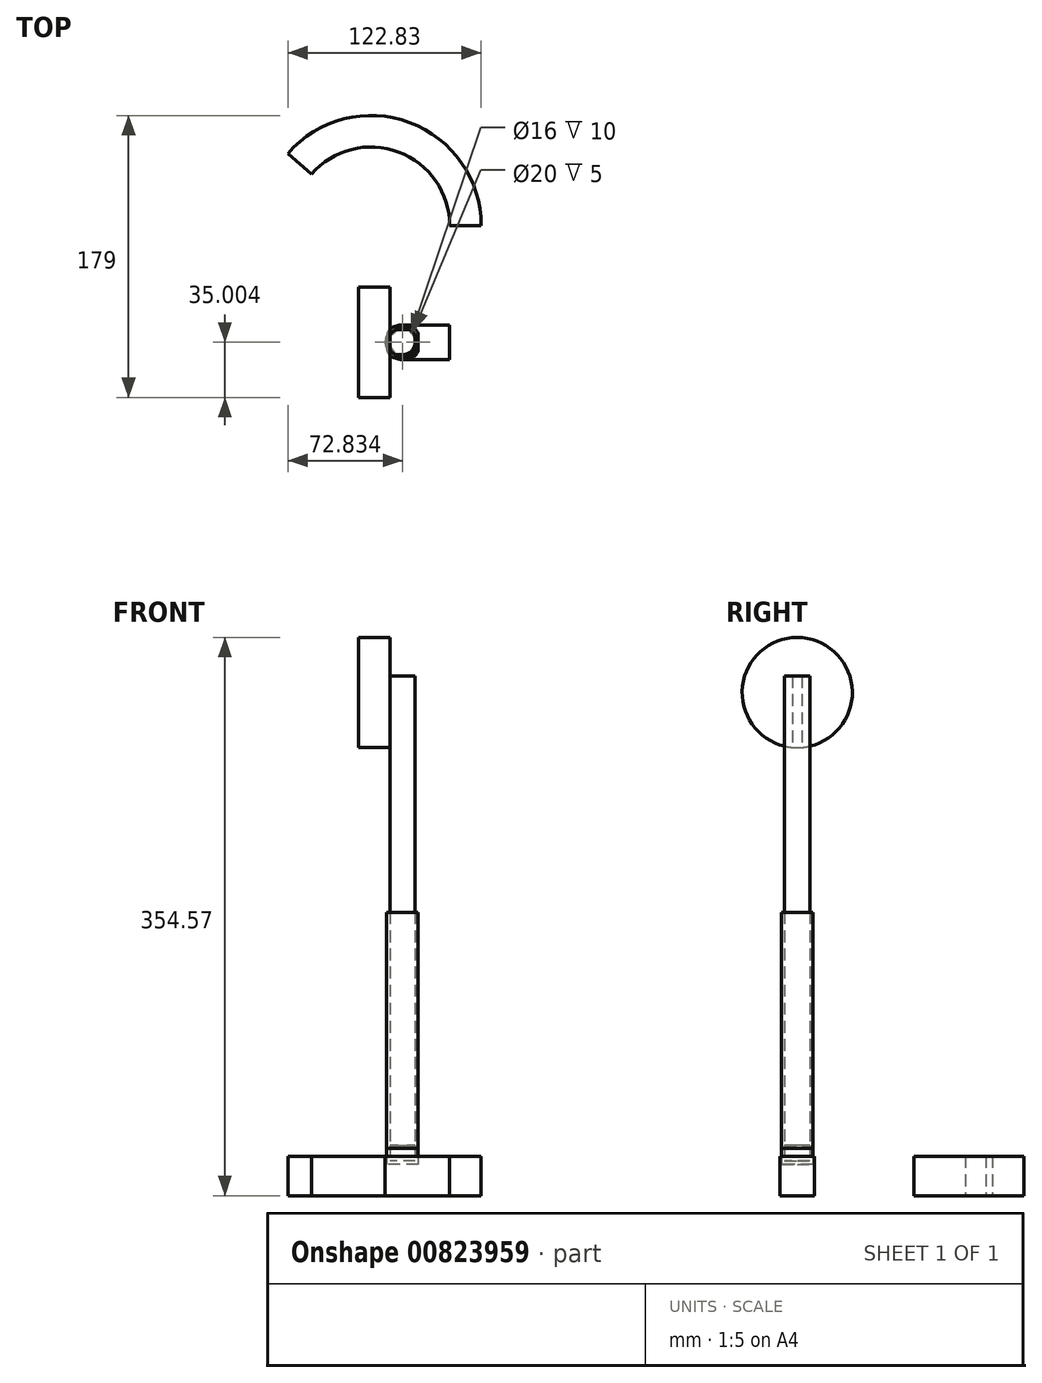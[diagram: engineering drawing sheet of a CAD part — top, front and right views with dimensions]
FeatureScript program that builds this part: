
annotation { "Feature Type Name" : "Feature", "Feature Type Description" : "" }
export const myFeature = defineFeature(function(context is Context, id is Id, definition is map)
    precondition{}
    {
        {
            var Q0;
            Q0=qCreatedBy(makeId("Top.planeOp"),FACE);
            var sketch = newSketch(context, id + "F0", { "sketchPlane" : qUnion([Q0])});
            skLineSegment(sketch, "E0.bottom", {"start": v(17.96, 119.9) * mm, "end": v(67.96, 119.9) * mm});
            skLineSegment(sketch, "E0.left", {"start": v(17.96, 119.9) * mm, "end": v(17.96, -30.1) * mm});
            skLineSegment(sketch, "E0.right", {"start": v(117.96, 119.9) * mm, "end": v(117.96, -30.1) * mm});
            skArc(sketch, "E1", {"start": v(117.96, 119.9) * mm, "mid": v(85.47, 166.74) * mm, "end": v(30.23, 152.7) * mm});
            skArc(sketch, "E2.MirrorCS", {"start": v(117.96, -30.1) * mm, "mid": v(85.47, -76.93) * mm, "end": v(30.23, -62.9) * mm});
            skArc(sketch, "E3.0", {"start": v(137.96, 119.9) * mm, "mid": v(92.48, 185.47) * mm, "end": v(15.13, 165.83) * mm});
            skLineSegment(sketch, "E3.1", {"start": v(137.96, 119.9) * mm, "end": v(137.96, -30.1) * mm});
            skArc(sketch, "E3.2", {"start": v(137.96, -30.1) * mm, "mid": v(92.48, -95.66) * mm, "end": v(15.13, -76.02) * mm});
            skLineSegment(sketch, "E4", {"start": v(67.96, 119.9) * mm, "end": v(-3.53, 182.05) * mm});
            skLineSegment(sketch, "E5.MirrorCS", {"start": v(67.96, -30.1) * mm, "end": v(-3.53, -92.24) * mm});
            skLineSegment(sketch, "E6.trimOffspring", {"start": v(117.96, 119.9) * mm, "end": v(137.96, 119.9) * mm});
            skArc(sketch, "E7", {"start": v(87.96, 56.9) * mm, "mid": v(76.96, 45.9) * mm, "end": v(87.96, 34.9) * mm});
            skLineSegment(sketch, "E8", {"start": v(117.96, 56.9) * mm, "end": v(87.96, 56.9) * mm});
            skLineSegment(sketch, "E9", {"start": v(117.96, 34.9) * mm, "end": v(87.96, 34.9) * mm});
            skCircle(sketch, "E10", {"center": v(87.96, 45.9) * mm, "radius": 11 * mm});
            skSolve(sketch);
        }
        {
            var Q0;
            {var subQ0=sQuery(id+"F0.wireOp",EDGE,"E1");Q0=makeQuery(id+"F0.imprint","IMPRINT",FACE,{"disambiguationData":[TD([[makeQuery(id+"F0.imprint","IMPRINT",EDGE,{"derivedFrom":subQ0}),-1.0]])]});}
            var Q1;
            {var subQ0=sQuery(id+"F0.wireOp",EDGE,"E2.MirrorCS");Q1=makeQuery(id+"F0.imprint","IMPRINT",FACE,{"disambiguationData":[TD([[makeQuery(id+"F0.imprint","IMPRINT",EDGE,{"derivedFrom":subQ0}),1.0]])]});}
            var Q2;
            {var subQ0=sQuery(id+"F0.wireOp",EDGE,"E8");Q2=makeQuery(id+"F0.imprint","IMPRINT",FACE,{"disambiguationData":[TD([[makeQuery(id+"F0.imprint","IMPRINT",EDGE,{"derivedFrom":subQ0}),1.0]])]});}
            var Q3;
            {var subQ0=sQuery(id+"F0.wireOp",EDGE,"E10");var subQ1=makeQuery(id+"F0.imprint","INTERSECT",VERTEX,{"derivedFrom":[sQuery(id+"F0.wireOp",EDGE,"E8"),subQ0]});Q3=makeQuery(id+"F0.imprint","IMPRINT",FACE,{"disambiguationData":[TD([[makeQuery(id+"F0.imprint","IMPRINT",EDGE,{"disambiguationData":[TD([[subQ1,-1.0]])],"derivedFrom":subQ0}),1.0]])]});}
            extrude(context, id + "F1", {"entities" : qUnion([Q0, Q1, Q2, Q3]), "depth" : 25 * mm, "offsetDistance" : 25 * mm});
        }
        {
            var Q0;
            Q0=makeQuery(id+"F1.opExtrude","CAP_FACE",FACE,{"disambiguationData":[OSD([sQuery(id+"F0.wireOp",EDGE,"E0.right"),sQuery(id+"F0.wireOp",EDGE,"E1"),sQuery(id+"F0.wireOp",EDGE,"E2.MirrorCS"),sQuery(id+"F0.wireOp",EDGE,"E3.0"),sQuery(id+"F0.wireOp",EDGE,"E3.1"),sQuery(id+"F0.wireOp",EDGE,"E3.2"),sQuery(id+"F0.wireOp",EDGE,"E4"),sQuery(id+"F0.wireOp",EDGE,"E5.MirrorCS"),sQuery(id+"F0.wireOp",EDGE,"E8"),sQuery(id+"F0.wireOp",EDGE,"E9"),sQuery(id+"F0.wireOp",EDGE,"E10")])],"isStart":false});
            var sketch = newSketch(context, id + "F2", { "sketchPlane" : qUnion([Q0])});
            skCircle(sketch, "E11", {"center": v(87.96, 45.9) * mm, "radius": 10 * mm});
            skSolve(sketch);
        }
        {
            var Q0;
            Q0 = qSketchRegion(id + "F2", true);
            extrude(context, id + "F3", {"entities" : qUnion([Q0]), "operationType" : NewBodyOperationType.REMOVE, "oppositeDirection" : true, "depth" : 5 * mm, "offsetDistance" : 25 * mm});
        }
        {
            var Q0;
            Q0=makeQuery(id+"F3.boolean.opBoolean","COPY",FACE,{"derivedFrom":makeQuery(id+"F3.opExtrude","CAP_FACE",FACE,{"disambiguationData":[OSD([sQuery(id+"F2.wireOp",EDGE,"E11")])],"isStart":false})});
            var sketch = newSketch(context, id + "F4", { "sketchPlane" : qUnion([Q0])});
            skSolve(sketch);
        }
        {
            var Q0;
            Q0 = qSketchRegion(id + "F4", true);
            var Q1;
            Q1=makeQuery(id+"F4.imprint","IMPRINT",FACE,{"disambiguationData":[TD([[makeQuery(id+"F4.imprint","IMPRINT",EDGE,{"derivedFrom":makeQuery(id+"F3.boolean.opBoolean","COPY",EDGE,{"derivedFrom":makeQuery(id+"F3.opExtrude","CAP_EDGE",EDGE,{"disambiguationData":[OSD([sQuery(id+"F2.wireOp",EDGE,"E11")])],"isStart":false})})}),1.0]])]});
            extrude(context, id + "F5", {"entities" : qUnion([Q0, Q1]), "depth" : 10 * mm, "offsetDistance" : 25 * mm});
        }
        {
            var Q0;
            Q0=makeQuery(id+"F5.opExtrude","CAP_FACE",FACE,{"disambiguationData":[OSD([sQuery(id+"F2.wireOp",EDGE,"E11")])],"isStart":false});
            var sketch = newSketch(context, id + "F6", { "sketchPlane" : qUnion([Q0])});
            skLineSegment(sketch, "E12.bottom", {"start": v(77.96, 55.9) * mm, "end": v(97.96, 55.9) * mm});
            skLineSegment(sketch, "E12.top", {"start": v(77.96, 35.9) * mm, "end": v(97.96, 35.9) * mm});
            skLineSegment(sketch, "E12.left", {"start": v(77.96, 55.9) * mm, "end": v(77.96, 35.9) * mm});
            skLineSegment(sketch, "E12.right", {"start": v(97.96, 55.9) * mm, "end": v(97.96, 35.9) * mm});
            skCircle(sketch, "E13", {"center": v(87.96, 45.9) * mm, "radius": 10 * mm});
            skSolve(sketch);
        }
        {
            var Q0;
            {var subQ0=sQuery(id+"F6.wireOp",EDGE,"E12.right");var subQ1=sQuery(id+"F6.wireOp",EDGE,"E12.bottom");var subQ2=makeQuery(id+"F6.imprint","INTERSECT",VERTEX,{"derivedFrom":[subQ1,subQ0]});Q0=makeQuery(id+"F6.imprint","IMPRINT",FACE,{"disambiguationData":[TD([[makeQuery(id+"F6.imprint","IMPRINT",EDGE,{"disambiguationData":[TD([[subQ2,1.0]])],"derivedFrom":subQ1}),-1.0]])]});}
            var Q1;
            {var subQ0=sQuery(id+"F6.wireOp",EDGE,"E13");var subQ1=makeQuery(id+"F6.imprint","INTERSECT",VERTEX,{"derivedFrom":[sQuery(id+"F6.wireOp",EDGE,"E12.bottom"),subQ0]});Q1=makeQuery(id+"F6.imprint","IMPRINT",FACE,{"disambiguationData":[TD([[makeQuery(id+"F6.imprint","IMPRINT",EDGE,{"disambiguationData":[TD([[subQ1,1.0]])],"derivedFrom":subQ0}),1.0]])]});}
            var Q2;
            {var subQ0=sQuery(id+"F6.wireOp",EDGE,"E12.left");var subQ1=sQuery(id+"F6.wireOp",EDGE,"E12.bottom");var subQ2=makeQuery(id+"F6.imprint","INTERSECT",VERTEX,{"derivedFrom":[subQ1,subQ0]});Q2=makeQuery(id+"F6.imprint","IMPRINT",FACE,{"disambiguationData":[TD([[makeQuery(id+"F6.imprint","IMPRINT",EDGE,{"disambiguationData":[TD([[subQ2,-1.0]])],"derivedFrom":subQ1}),-1.0]])]});}
            var Q3;
            {var subQ0=sQuery(id+"F6.wireOp",EDGE,"E12.left");var subQ1=sQuery(id+"F6.wireOp",EDGE,"E12.top");var subQ2=makeQuery(id+"F6.imprint","INTERSECT",VERTEX,{"derivedFrom":[subQ1,subQ0]});Q3=makeQuery(id+"F6.imprint","IMPRINT",FACE,{"disambiguationData":[TD([[makeQuery(id+"F6.imprint","IMPRINT",EDGE,{"disambiguationData":[TD([[subQ2,-1.0]])],"derivedFrom":subQ1}),1.0]])]});}
            var Q4;
            {var subQ0=sQuery(id+"F6.wireOp",EDGE,"E12.right");var subQ1=sQuery(id+"F6.wireOp",EDGE,"E12.top");var subQ2=makeQuery(id+"F6.imprint","INTERSECT",VERTEX,{"derivedFrom":[subQ1,subQ0]});Q4=makeQuery(id+"F6.imprint","IMPRINT",FACE,{"disambiguationData":[TD([[makeQuery(id+"F6.imprint","IMPRINT",EDGE,{"disambiguationData":[TD([[subQ2,1.0]])],"derivedFrom":subQ1}),1.0]])]});}
            extrude(context, id + "F7", {"entities" : qUnion([Q0, Q1, Q2, Q3, Q4]), "operationType" : NewBodyOperationType.ADD, "depth" : 150 * mm, "offsetDistance" : 25 * mm});
        }
        {
            var Q0;
            Q0=makeQuery(id+"F7.opExtrude","CAP_FACE",FACE,{"disambiguationData":[OSD([sQuery(id+"F6.wireOp",EDGE,"E12.bottom"),sQuery(id+"F6.wireOp",EDGE,"E12.top"),sQuery(id+"F6.wireOp",EDGE,"E12.left"),sQuery(id+"F6.wireOp",EDGE,"E12.right")])],"isStart":false});
            shell(context, id + "F8", {"entities" : qUnion([Q0]), "thickness" : 2 * mm});
        }
        {
            var Q0;
            Q0=makeQuery(id+"F7.opExtrude","SWEPT_EDGE",EDGE,{"disambiguationData":[OSD([sQuery(id+"F6.wireOp",EDGE,"E12.top"),sQuery(id+"F6.wireOp",EDGE,"E12.right")])]});
            var Q1;
            Q1=makeQuery(id+"F7.opExtrude","SWEPT_EDGE",EDGE,{"disambiguationData":[OSD([sQuery(id+"F6.wireOp",EDGE,"E12.top"),sQuery(id+"F6.wireOp",EDGE,"E12.left")])]});
            var Q2;
            Q2=makeQuery(id+"F7.opExtrude","SWEPT_EDGE",EDGE,{"disambiguationData":[OSD([sQuery(id+"F6.wireOp",EDGE,"E12.bottom"),sQuery(id+"F6.wireOp",EDGE,"E12.left")])]});
            var Q3;
            Q3=makeQuery(id+"F7.opExtrude","SWEPT_EDGE",EDGE,{"disambiguationData":[OSD([sQuery(id+"F6.wireOp",EDGE,"E12.bottom"),sQuery(id+"F6.wireOp",EDGE,"E12.right")])]});
            fillet(context, id + "F9", {"entities" : qUnion([Q0, Q1, Q2, Q3]), "radius" : 6 * mm, "tangentPropagation" : true, "allowEdgeOverflow" : false});
        }
        {
            var Q0;
            Q0=makeQuery(id+"F7.opExtrude","CAP_FACE",FACE,{"disambiguationData":[OSD([sQuery(id+"F6.wireOp",EDGE,"E12.bottom"),sQuery(id+"F6.wireOp",EDGE,"E12.top"),sQuery(id+"F6.wireOp",EDGE,"E12.left"),sQuery(id+"F6.wireOp",EDGE,"E12.right")])],"isStart":false});
            var sketch = newSketch(context, id + "F10", { "sketchPlane" : qUnion([Q0])});
            skSolve(sketch);
        }
        {
            var Q0;
            Q0=makeQuery(id+"F8.opShell","OFFSET_EDGE",EDGE,{"disambiguationData":[OSD([sQuery(id+"F6.wireOp",EDGE,"E12.bottom"),sQuery(id+"F6.wireOp",EDGE,"E12.right")])]});
            var Q1;
            Q1=makeQuery(id+"F8.opShell","OFFSET_EDGE",EDGE,{"disambiguationData":[OSD([sQuery(id+"F6.wireOp",EDGE,"E12.top"),sQuery(id+"F6.wireOp",EDGE,"E12.left")])]});
            var Q2;
            Q2=makeQuery(id+"F8.opShell","OFFSET_EDGE",EDGE,{"disambiguationData":[OSD([sQuery(id+"F6.wireOp",EDGE,"E12.bottom"),sQuery(id+"F6.wireOp",EDGE,"E12.left")])]});
            var Q3;
            Q3=makeQuery(id+"F8.opShell","OFFSET_EDGE",EDGE,{"disambiguationData":[OSD([sQuery(id+"F6.wireOp",EDGE,"E12.top"),sQuery(id+"F6.wireOp",EDGE,"E12.right")])]});
            fillet(context, id + "F11", {"entities" : qUnion([Q0, Q1, Q2, Q3]), "radius" : 5 * mm, "tangentPropagation" : true, "allowEdgeOverflow" : false});
        }
        {
            var Q0;
            {var subQ2=sQuery(id+"F6.wireOp",EDGE,"E12.bottom");var subQ3=makeQuery(id+"F7.opExtrude","CAP_EDGE",EDGE,{"disambiguationData":[OSD([subQ2])],"isStart":false});Q0=makeQuery(id+"F10.imprint","IMPRINT",FACE,{"disambiguationData":[TD([[makeQuery(id+"F10.imprint","IMPRINT",EDGE,{"derivedFrom":subQ3}),-1.0]])]});}
            var sketch = newSketch(context, id + "F12", { "sketchPlane" : qUnion([Q0])});
            skLineSegment(sketch, "E14.bottom", {"start": v(84.96, 53.9) * mm, "end": v(90.96, 53.9) * mm});
            skLineSegment(sketch, "E14.top", {"start": v(84.96, 37.9) * mm, "end": v(90.96, 37.9) * mm});
            skLineSegment(sketch, "E14.left", {"start": v(79.96, 48.9) * mm, "end": v(79.96, 42.9) * mm});
            skLineSegment(sketch, "E14.right", {"start": v(95.96, 48.9) * mm, "end": v(95.96, 42.9) * mm});
            skPoint(sketch, "E15.visualSharp", {"position": v(79.96, 37.9) * mm});
            skArc(sketch, "E15.filletArc", {"start": v(79.96, 42.9) * mm, "mid": v(81.43, 39.37) * mm, "end": v(84.96, 37.9) * mm});
            skPoint(sketch, "E16.visualSharp", {"position": v(95.96, 37.9) * mm});
            skArc(sketch, "E16.filletArc", {"start": v(90.96, 37.9) * mm, "mid": v(94.5, 39.37) * mm, "end": v(95.96, 42.9) * mm});
            skPoint(sketch, "E17.visualSharp", {"position": v(95.96, 53.9) * mm});
            skArc(sketch, "E17.filletArc", {"start": v(95.96, 48.9) * mm, "mid": v(94.5, 52.44) * mm, "end": v(90.96, 53.9) * mm});
            skPoint(sketch, "E18.visualSharp", {"position": v(79.96, 53.9) * mm});
            skArc(sketch, "E18.filletArc", {"start": v(84.96, 53.9) * mm, "mid": v(81.43, 52.44) * mm, "end": v(79.96, 48.9) * mm});
            skSolve(sketch);
        }
        {
            var Q0;
            Q0 = qSketchRegion(id + "F12", true);
            var Q1;
            Q1 = qSketchRegion(id + "F14", true);
            extrude(context, id + "F13", {"entities" : qUnion([Q0, Q1]), "depth" : 150 * mm, "offsetDistance" : 25 * mm});
        }
        {
            var Q0;
            Q0=makeQuery(id+"F13.opExtrude","SWEPT_FACE",FACE,{"disambiguationData":[OSD([sQuery(id+"F12.wireOp",EDGE,"E14.left")])]});
            var sketch = newSketch(context, id + "F14", { "sketchPlane" : qUnion([Q0])});
            skCircle(sketch, "E19", {"center": v(-45.9, 319.57) * mm, "radius": 35 * mm});
            skPoint(sketch, "E20", {"position": v(-45.9, 330) * mm});
            skSolve(sketch);
        }
        {
            var Q0;
            {var subQ1=sQuery(id+"F12.wireOp",EDGE,"E14.left");var subQ7=makeQuery(id+"F13.opExtrude","CAP_EDGE",EDGE,{"disambiguationData":[OSD([subQ1])],"isStart":false});Q0=makeQuery(id+"F14.imprint","IMPRINT",FACE,{"disambiguationData":[TD([[makeQuery(id+"F14.imprint","IMPRINT",EDGE,{"derivedFrom":subQ7}),1.0]])]});}
            var Q1;
            {var subQ1=sQuery(id+"F12.wireOp",EDGE,"E14.left");var subQ7=makeQuery(id+"F13.opExtrude","CAP_EDGE",EDGE,{"disambiguationData":[OSD([subQ1])],"isStart":false});Q1=makeQuery(id+"F14.imprint","IMPRINT",FACE,{"disambiguationData":[TD([[makeQuery(id+"F14.imprint","IMPRINT",EDGE,{"derivedFrom":subQ7}),-1.0]])]});}
            extrude(context, id + "F15", {"entities" : qUnion([Q0, Q1]), "operationType" : NewBodyOperationType.ADD, "depth" : 20 * mm, "offsetDistance" : 25 * mm});
        }
    });
